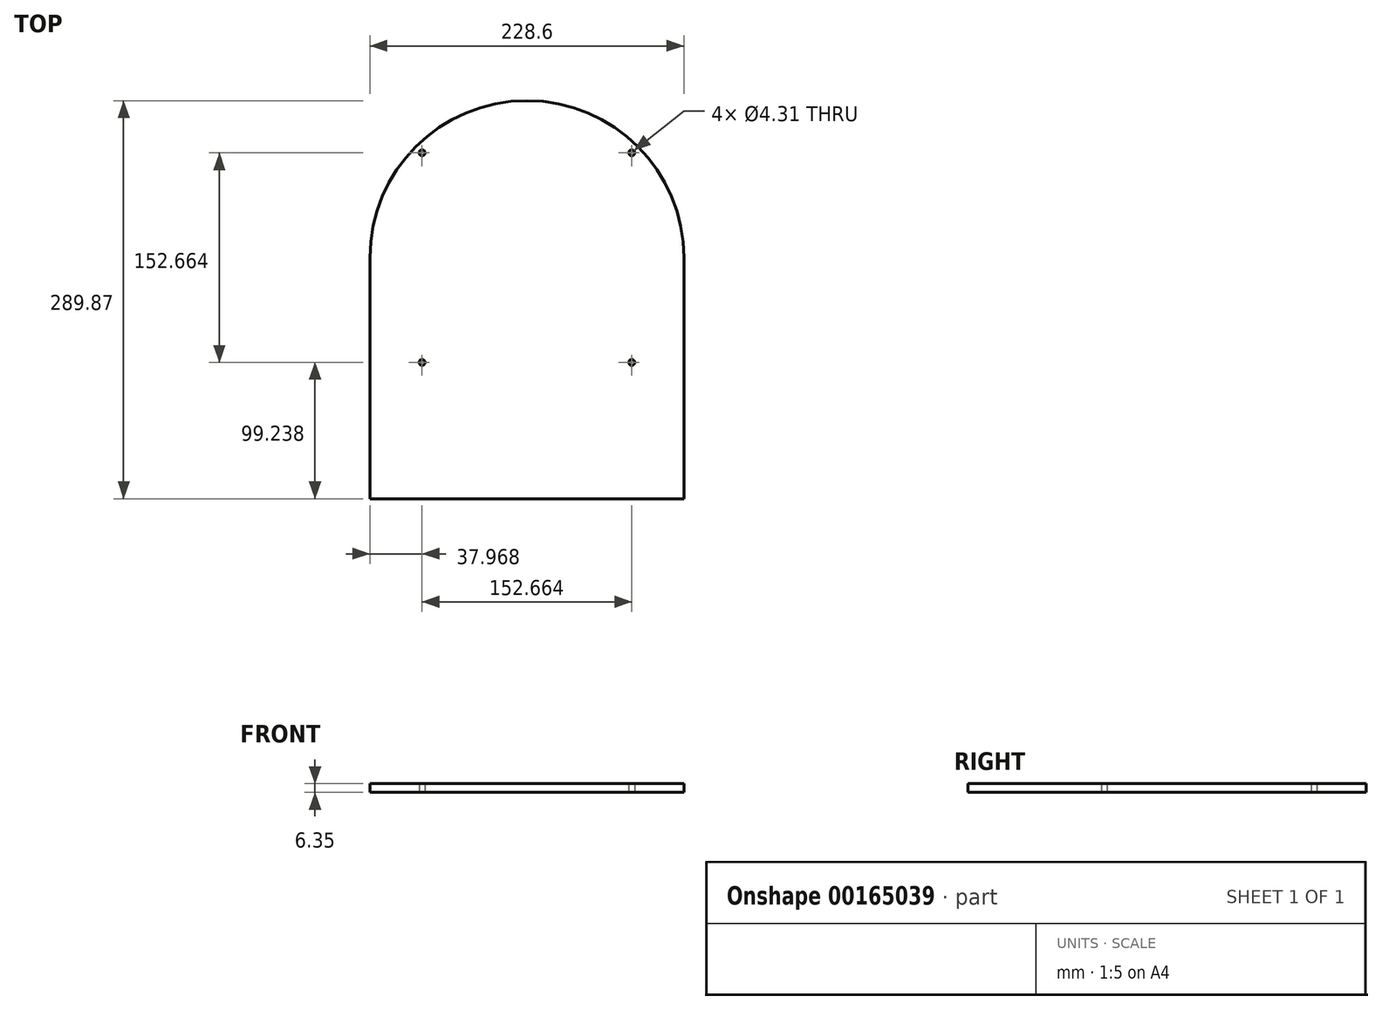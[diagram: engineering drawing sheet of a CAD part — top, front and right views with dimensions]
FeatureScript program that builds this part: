
annotation { "Feature Type Name" : "Feature", "Feature Type Description" : "" }
export const myFeature = defineFeature(function(context is Context, id is Id, definition is map)
    precondition{}
    {
        {
            var Q0;
            Q0=qCreatedBy(makeId("Top.planeOp"),FACE);
            var sketch = newSketch(context, id + "F0", { "sketchPlane" : qUnion([Q0])});
            skLineSegment(sketch, "E0.bottom", {"start": v(0, 0) * mm, "end": v(-228.6, 0) * mm, "construction": true});
            skLineSegment(sketch, "E0.top", {"start": v(0, -175.57) * mm, "end": v(-228.6, -175.57) * mm});
            skLineSegment(sketch, "E0.left", {"start": v(0, 0) * mm, "end": v(0, -175.57) * mm});
            skLineSegment(sketch, "E0.right", {"start": v(-228.6, 0) * mm, "end": v(-228.6, -175.57) * mm});
            skArc(sketch, "E1", {"start": v(0, 0) * mm, "mid": v(-114.3, 114.3) * mm, "end": v(-228.6, 0) * mm});
            skLineSegment(sketch, "E2.bottom", {"start": v(-37.97, 76.33) * mm, "end": v(-190.63, 76.33) * mm, "construction": true});
            skLineSegment(sketch, "E2.top", {"start": v(-37.97, -76.33) * mm, "end": v(-190.63, -76.33) * mm, "construction": true});
            skLineSegment(sketch, "E2.left", {"start": v(-37.97, 76.33) * mm, "end": v(-37.97, -76.33) * mm, "construction": true});
            skLineSegment(sketch, "E2.right", {"start": v(-190.63, 76.33) * mm, "end": v(-190.63, -76.33) * mm, "construction": true});
            skCircle(sketch, "E3", {"center": v(-37.97, 76.33) * mm, "radius": 6.35 * mm, "construction": true});
            skCircle(sketch, "E4", {"center": v(-190.63, 76.33) * mm, "radius": 2.15 * mm});
            skCircle(sketch, "E5", {"center": v(-37.97, 76.33) * mm, "radius": 2.15 * mm});
            skCircle(sketch, "E6", {"center": v(-37.97, -76.33) * mm, "radius": 2.15 * mm});
            skCircle(sketch, "E7", {"center": v(-190.63, -76.33) * mm, "radius": 2.15 * mm});
            skSolve(sketch);
        }
        {
            var Q0;
            Q0 = qSketchRegion(id + "F0", true);
            extrude(context, id + "F1", {"entities" : qUnion([Q0]), "depth" : 6.35 * mm});
        }
    });
